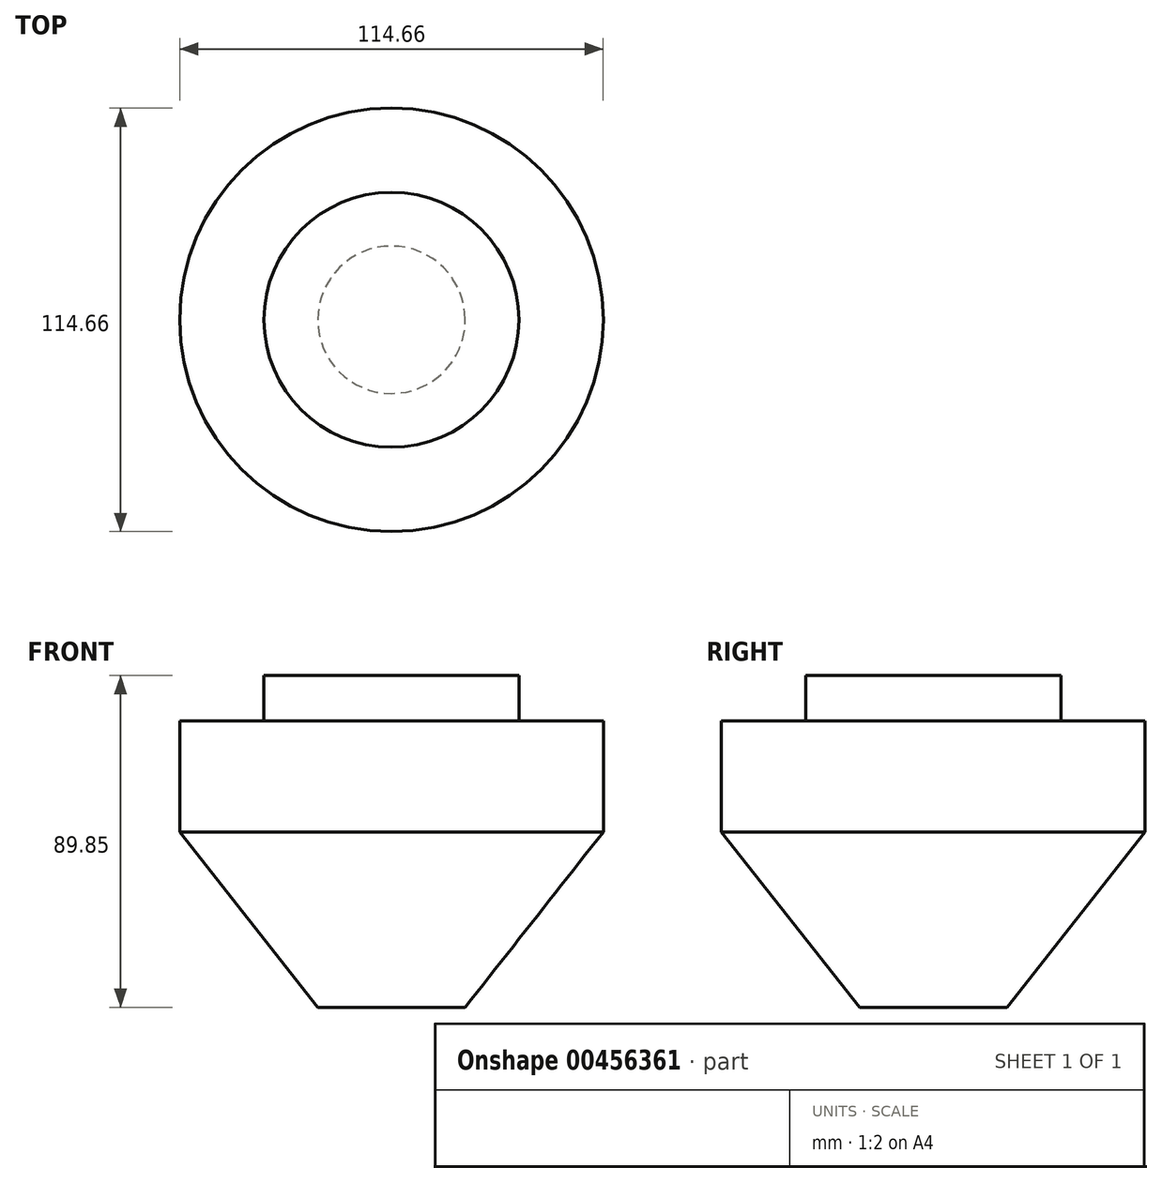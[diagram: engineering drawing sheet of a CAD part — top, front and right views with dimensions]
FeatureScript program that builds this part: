
annotation { "Feature Type Name" : "Feature", "Feature Type Description" : "" }
export const myFeature = defineFeature(function(context is Context, id is Id, definition is map)
    precondition{}
    {
        {
            var Q0;
            Q0=qCreatedBy(makeId("Front.planeOp"),FACE);
            var sketch = newSketch(context, id + "F0", { "sketchPlane" : qUnion([Q0])});
            skLineSegment(sketch, "E0", {"start": v(0, 42.36) * mm, "end": v(34.51, 42.36) * mm});
            skLineSegment(sketch, "E1", {"start": v(34.51, 42.36) * mm, "end": v(34.51, 30.1) * mm});
            skLineSegment(sketch, "E2", {"start": v(34.51, 30.1) * mm, "end": v(57.33, 30.1) * mm});
            skLineSegment(sketch, "E3", {"start": v(57.33, 30.1) * mm, "end": v(57.33, 0) * mm});
            skLineSegment(sketch, "E4", {"start": v(57.33, 0) * mm, "end": v(19.97, -47.5) * mm});
            skLineSegment(sketch, "E5", {"start": v(19.97, -47.5) * mm, "end": v(0, -47.5) * mm});
            skPoint(sketch, "E6.MirrorCS.end.orphan", {"position": v(-34.51, 42.36) * mm});
            skPoint(sketch, "E6.MirrorCS.start.orphan", {"position": v(0, 42.36) * mm});
            skPoint(sketch, "E7.MirrorCS.end.orphan", {"position": v(-34.51, 30.1) * mm});
            skPoint(sketch, "E8.MirrorCS.end.orphan", {"position": v(-57.33, 30.1) * mm});
            skPoint(sketch, "E9.MirrorCS.end.orphan", {"position": v(-57.33, 0) * mm});
            skPoint(sketch, "E10.MirrorCS.end.orphan", {"position": v(-19.97, -47.5) * mm});
            skPoint(sketch, "E11.MirrorCS.end.orphan", {"position": v(0, -47.5) * mm});
            skLineSegment(sketch, "E12", {"start": v(0, 42.36) * mm, "end": v(0, 0) * mm});
            skLineSegment(sketch, "E13", {"start": v(0, 0) * mm, "end": v(0, -47.5) * mm});
            skSolve(sketch);
        }
        {
            var Q0;
            Q0 = qSketchRegion(id + "F0", true);
            var Q1;
            Q1=sQuery(id+"F0.wireOp",EDGE,"E12");
            revolve(context, id + "F1", {"entities" : qUnion([Q0]), "axis" : qUnion([Q1]), "revolveType" : RevolveType.FULL});
        }
    });
